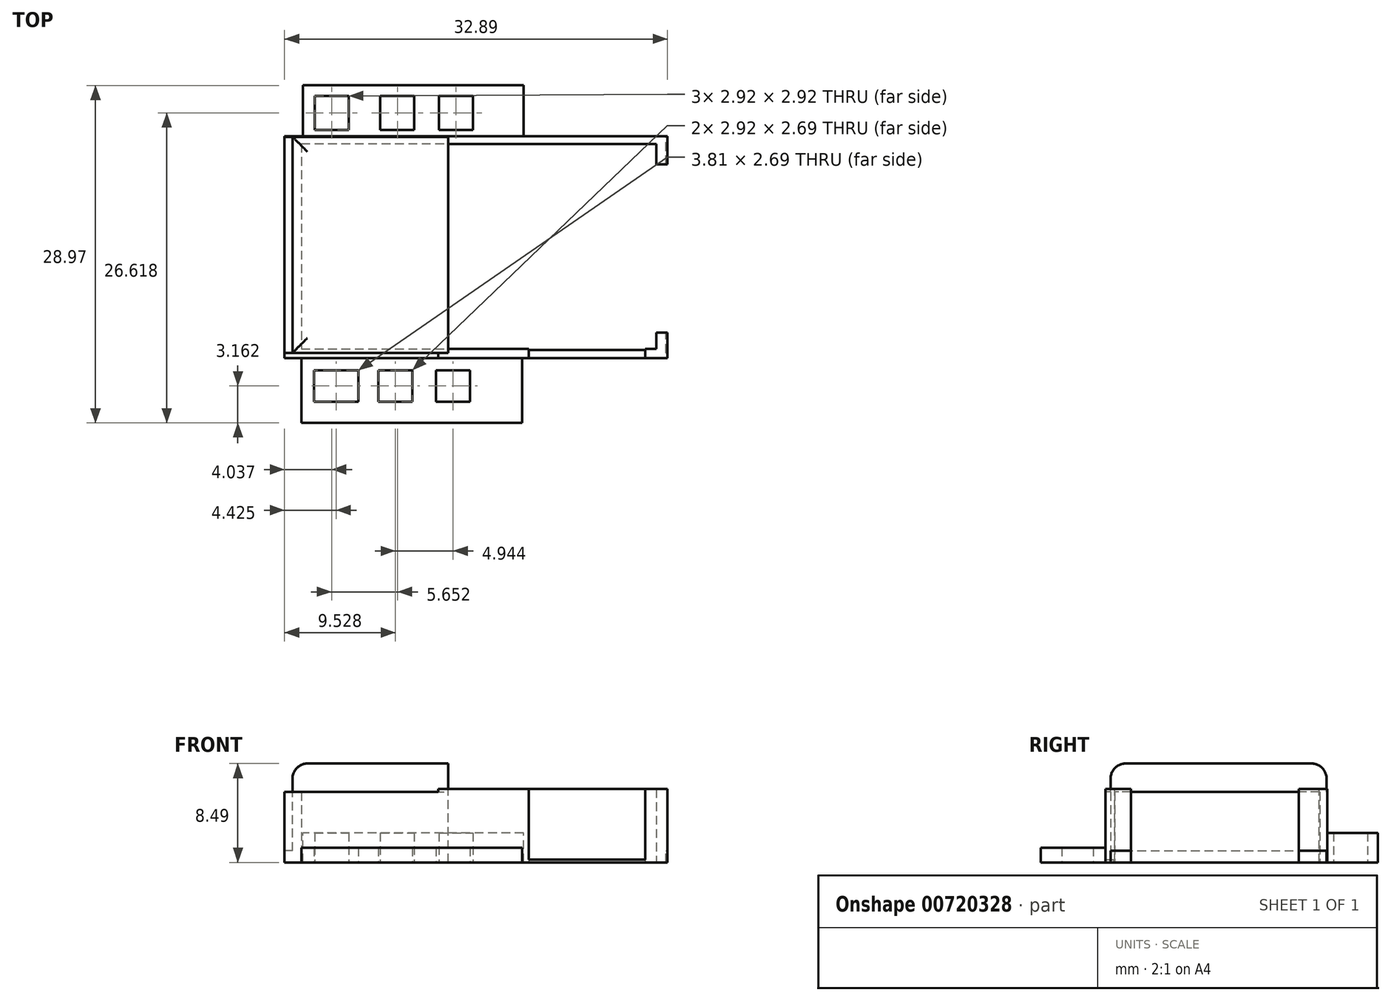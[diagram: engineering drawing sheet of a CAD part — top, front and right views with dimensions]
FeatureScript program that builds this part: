
annotation { "Feature Type Name" : "Feature", "Feature Type Description" : "" }
export const myFeature = defineFeature(function(context is Context, id is Id, definition is map)
    precondition{}
    {
        {
            var Q0;
            Q0=qCreatedBy(makeId("Top.planeOp"),FACE);
            var sketch = newSketch(context, id + "F0", { "sketchPlane" : qUnion([Q0])});
            skLineSegment(sketch, "E0.bottom", {"start": v(0, 0) * mm, "end": v(-33.73, 0) * mm});
            skLineSegment(sketch, "E0.top", {"start": v(0, 18.54) * mm, "end": v(-33.73, 18.54) * mm});
            skLineSegment(sketch, "E0.left", {"start": v(0, 0) * mm, "end": v(0, 18.54) * mm});
            skLineSegment(sketch, "E0.right", {"start": v(-33.73, 0) * mm, "end": v(-33.73, 18.54) * mm});
            skSolve(sketch);
        }
        {
            var Q0;
            Q0=makeQuery(id+"F0.imprint","IMPRINT",FACE,{"disambiguationData":[TD([[makeQuery(id+"F0.imprint","IMPRINT",EDGE,{"derivedFrom":sQuery(id+"F0.wireOp",EDGE,"E0.bottom")}),-1.0]])]});
            extrude(context, id + "F1", {"entities" : qUnion([Q0]), "depth" : 1 * mm, "offsetDistance" : 25.4 * mm});
        }
        {
            var Q0;
            Q0=qCreatedBy(makeId("Top.planeOp"),FACE);
            var sketch = newSketch(context, id + "F2", { "sketchPlane" : qUnion([Q0])});
            skLineSegment(sketch, "E1", {"start": v(0, 18.18) * mm, "end": v(-0.25, 18.18) * mm});
            skLineSegment(sketch, "E2", {"start": v(0, 0) * mm, "end": v(-1.24, 0) * mm});
            skLineSegment(sketch, "E3.bottom", {"start": v(-0.25, 16.18) * mm, "end": v(-2.75, 16.18) * mm});
            skLineSegment(sketch, "E3.top", {"start": v(-0.25, 1.75) * mm, "end": v(-2.75, 1.75) * mm});
            skLineSegment(sketch, "E3.left", {"start": v(-0.25, 16.18) * mm, "end": v(-0.25, 1.75) * mm});
            skLineSegment(sketch, "E3.right", {"start": v(-2.75, 16.18) * mm, "end": v(-2.75, 1.75) * mm});
            skSolve(sketch);
        }
        {
            var Q0;
            Q0 = qSketchRegion(id + "F2", true);
            extrude(context, id + "F3", {"entities" : qUnion([Q0]), "operationType" : NewBodyOperationType.ADD, "depth" : 7 * mm, "offsetDistance" : 25.4 * mm});
        }
        {
            var Q0;
            Q0=makeQuery(id+"F1.opExtrude","CAP_FACE",FACE,{"disambiguationData":[OSD([sQuery(id+"F0.wireOp",EDGE,"E0.bottom"),sQuery(id+"F0.wireOp",EDGE,"E0.top"),sQuery(id+"F0.wireOp",EDGE,"E0.left"),sQuery(id+"F0.wireOp",EDGE,"E0.right")])],"isStart":false});
            var sketch = newSketch(context, id + "F4", { "sketchPlane" : qUnion([Q0])});
            skLineSegment(sketch, "E4", {"start": v(0, 0) * mm, "end": v(-2.75, 0) * mm});
            skLineSegment(sketch, "E5.bottom", {"start": v(-2.75, 0) * mm, "end": v(-12.75, 0) * mm});
            skLineSegment(sketch, "E5.top", {"start": v(-2.75, 3) * mm, "end": v(-12.75, 3) * mm});
            skLineSegment(sketch, "E5.left", {"start": v(-2.75, 0) * mm, "end": v(-2.75, 3) * mm});
            skLineSegment(sketch, "E5.right", {"start": v(-12.75, 0) * mm, "end": v(-12.75, 3) * mm});
            skLineSegment(sketch, "E6", {"start": v(-2.75, 3) * mm, "end": v(-2.75, 4) * mm});
            skLineSegment(sketch, "E7", {"start": v(-12.75, 3) * mm, "end": v(-7.75, 3) * mm});
            skSolve(sketch);
        }
        {
            var Q0;
            {var subQ3=sQuery(id+"F4.wireOp",EDGE,"E5.bottom");Q0=makeQuery(id+"F4.imprint","IMPRINT",FACE,{"disambiguationData":[TD([[makeQuery(id+"F4.imprint","IMPRINT",EDGE,{"derivedFrom":subQ3}),-1.0]])]});}
            extrude(context, id + "F5", {"entities" : qUnion([Q0]), "operationType" : NewBodyOperationType.ADD, "depth" : 7.5 * mm, "offsetDistance" : 25.4 * mm});
        }
        {
            var Q0;
            Q0=makeQuery(id+"F1.opExtrude","CAP_FACE",FACE,{"disambiguationData":[OSD([sQuery(id+"F0.wireOp",EDGE,"E0.bottom"),sQuery(id+"F0.wireOp",EDGE,"E0.top"),sQuery(id+"F0.wireOp",EDGE,"E0.left"),sQuery(id+"F0.wireOp",EDGE,"E0.right")])],"isStart":false});
            var sketch = newSketch(context, id + "F6", { "sketchPlane" : qUnion([Q0])});
            skLineSegment(sketch, "E8", {"start": v(0, 18.54) * mm, "end": v(-2.73, 18.54) * mm});
            skLineSegment(sketch, "E9.bottom", {"start": v(-2.73, 18.54) * mm, "end": v(-8.73, 18.54) * mm});
            skLineSegment(sketch, "E9.top", {"start": v(-2.73, 15.54) * mm, "end": v(-8.73, 15.54) * mm});
            skLineSegment(sketch, "E9.left", {"start": v(-2.73, 18.54) * mm, "end": v(-2.73, 15.54) * mm});
            skLineSegment(sketch, "E9.right", {"start": v(-8.73, 18.54) * mm, "end": v(-8.73, 15.54) * mm});
            skSolve(sketch);
        }
        {
            var Q0;
            Q0 = qSketchRegion(id + "F6", true);
            extrude(context, id + "F7", {"entities" : qUnion([Q0]), "operationType" : NewBodyOperationType.ADD, "depth" : 3.75 * mm, "offsetDistance" : 25.4 * mm});
        }
        {
            var Q0;
            {var subQ0=sQuery(id+"F0.wireOp",EDGE,"E0.top");var subQ1=sQuery(id+"F0.wireOp",EDGE,"E0.right");var subQ2=sQuery(id+"F0.wireOp",EDGE,"E0.bottom");Q0=makeQuery(id+"F7.boolean.opBoolean","SPLIT",FACE,{"disambiguationData":[TD([makeQuery(id+"F1.opExtrude","SWEPT_FACE",FACE,{"disambiguationData":[OSD([subQ1])]})])],"derivedFrom":makeQuery(id+"F1.opExtrude","CAP_FACE",FACE,{"disambiguationData":[OSD([subQ2,subQ0,sQuery(id+"F0.wireOp",EDGE,"E0.left"),subQ1])],"isStart":false})});}
            var sketch = newSketch(context, id + "F8", { "sketchPlane" : qUnion([Q0])});
            skLineSegment(sketch, "E10", {"start": v(-12.75, 3) * mm, "end": v(-8.75, 3) * mm});
            skLineSegment(sketch, "E11.bottom", {"start": v(-8.75, 3) * mm, "end": v(-14.75, 3) * mm});
            skLineSegment(sketch, "E11.top", {"start": v(-8.75, 6.75) * mm, "end": v(-14.75, 6.75) * mm});
            skLineSegment(sketch, "E11.left", {"start": v(-8.75, 3) * mm, "end": v(-8.75, 6.75) * mm});
            skLineSegment(sketch, "E11.right", {"start": v(-14.75, 3) * mm, "end": v(-14.75, 6.75) * mm});
            skSolve(sketch);
        }
        {
            var Q0;
            Q0 = qSketchRegion(id + "F8", true);
            extrude(context, id + "F9", {"entities" : qUnion([Q0]), "operationType" : NewBodyOperationType.ADD, "depth" : 7.5 * mm, "offsetDistance" : 25.4 * mm});
        }
        {
            var Q0;
            {var subQ0=sQuery(id+"F0.wireOp",EDGE,"E0.top");var subQ1=sQuery(id+"F0.wireOp",EDGE,"E0.right");var subQ2=sQuery(id+"F0.wireOp",EDGE,"E0.bottom");Q0=makeQuery(id+"F7.boolean.opBoolean","SPLIT",FACE,{"disambiguationData":[TD([makeQuery(id+"F1.opExtrude","SWEPT_FACE",FACE,{"disambiguationData":[OSD([subQ1])]})])],"derivedFrom":makeQuery(id+"F1.opExtrude","CAP_FACE",FACE,{"disambiguationData":[OSD([subQ2,subQ0,sQuery(id+"F0.wireOp",EDGE,"E0.left"),subQ1])],"isStart":false})});}
            var sketch = newSketch(context, id + "F10", { "sketchPlane" : qUnion([Q0])});
            skLineSegment(sketch, "E12", {"start": v(-14.73, 7.77) * mm, "end": v(-9.77, 12.72) * mm});
            skLineSegment(sketch, "E13", {"start": v(-9.77, 12.72) * mm, "end": v(-14.73, 17.68) * mm});
            skLineSegment(sketch, "E14", {"start": v(-14.73, 17.68) * mm, "end": v(-19.68, 12.72) * mm});
            skLineSegment(sketch, "E15", {"start": v(-19.68, 12.72) * mm, "end": v(-14.73, 7.77) * mm});
            skSolve(sketch);
        }
        {
            var Q0;
            Q0=makeQuery(id+"F10.imprint","IMPRINT",FACE,{"disambiguationData":[TD([[makeQuery(id+"F10.imprint","IMPRINT",EDGE,{"derivedFrom":sQuery(id+"F10.wireOp",EDGE,"E12")}),1.0]])]});
            extrude(context, id + "F11", {"entities" : qUnion([Q0]), "operationType" : NewBodyOperationType.ADD, "depth" : 3 * mm, "offsetDistance" : 25.4 * mm});
        }
        {
            var Q0;
            Q0=makeQuery(id+"F9.boolean.opBoolean","MERGE",FACE,{"derivedFrom":[makeQuery(id+"F5.opExtrude","CAP_FACE",FACE,{"disambiguationData":[OSD([sQuery(id+"F4.wireOp",EDGE,"E5.bottom"),sQuery(id+"F4.wireOp",EDGE,"E5.top"),sQuery(id+"F4.wireOp",EDGE,"E5.left"),sQuery(id+"F4.wireOp",EDGE,"E5.right"),sQuery(id+"F4.wireOp",EDGE,"E7")])],"isStart":false}),makeQuery(id+"F9.opExtrude","CAP_FACE",FACE,{"disambiguationData":[OSD([sQuery(id+"F8.wireOp",EDGE,"E11.bottom"),sQuery(id+"F8.wireOp",EDGE,"E11.top"),sQuery(id+"F8.wireOp",EDGE,"E11.left"),sQuery(id+"F8.wireOp",EDGE,"E11.right")])],"isStart":false})]});
            var sketch = newSketch(context, id + "F12", { "sketchPlane" : qUnion([Q0])});
            skLineSegment(sketch, "E16", {"start": v(-14.75, 3) * mm, "end": v(-15.75, 3) * mm});
            skLineSegment(sketch, "E17", {"start": v(-14.75, 6.75) * mm, "end": v(-15.75, 6.75) * mm});
            skLineSegment(sketch, "E18", {"start": v(-15.75, 3) * mm, "end": v(-15.75, 0) * mm});
            skLineSegment(sketch, "E19", {"start": v(-15.75, 0) * mm, "end": v(-15.75, 3) * mm});
            skPoint(sketch, "E20.endSnap0", {"position": v(-7.75, 0) * mm});
            skSolve(sketch);
        }
        {
            var Q0;
            {var subQ0=sQuery(id+"F0.wireOp",EDGE,"E0.top");var subQ1=sQuery(id+"F0.wireOp",EDGE,"E0.right");var subQ2=sQuery(id+"F0.wireOp",EDGE,"E0.bottom");Q0=makeQuery(id+"F7.boolean.opBoolean","SPLIT",FACE,{"disambiguationData":[TD([makeQuery(id+"F1.opExtrude","SWEPT_FACE",FACE,{"disambiguationData":[OSD([subQ1])]})])],"derivedFrom":makeQuery(id+"F1.opExtrude","CAP_FACE",FACE,{"disambiguationData":[OSD([subQ2,subQ0,sQuery(id+"F0.wireOp",EDGE,"E0.left"),subQ1])],"isStart":false})});}
            var sketch = newSketch(context, id + "F13", { "sketchPlane" : qUnion([Q0])});
            skLineSegment(sketch, "E21", {"start": v(-19.68, 0) * mm, "end": v(-19.68, 18.54) * mm});
            skSolve(sketch);
        }
        {
            var Q0;
            Q0=sQuery(id+"F13.wireOp",EDGE,"E21");
            extrude(context, id + "F14", {"bodyType" : ToolBodyType.SURFACE, "surfaceEntities" : qUnion([Q0]), "depth" : 7.5 * mm, "offsetDistance" : 25.4 * mm});
        }
        {
            var Q0;
            Q0=makeQuery(id+"F14.opExtrude","SWEPT_FACE",FACE,{"disambiguationData":[OSD([sQuery(id+"F13.wireOp",EDGE,"E21")])]});
            var Q1;
            Q1=makeQuery(id+"F11.opExtrude","SWEPT_FACE",FACE,{"disambiguationData":[OSD([sQuery(id+"F10.wireOp",EDGE,"E15")])]});
            extrude(context, id + "F15", {"entities" : qUnion([Q0, Q1]), "operationType" : NewBodyOperationType.ADD, "oppositeDirection" : true, "depth" : 13.36 * mm, "offsetDistance" : 25.4 * mm});
        }
        {
            var Q0;
            {var subQ0=sQuery(id+"F13.wireOp",EDGE,"E21");Q0=makeQuery(id+"F15.opExtrude","CAP_EDGE",EDGE,{"disambiguationData":[OSD([subQ0]),TDD([makeQuery(id+"F14.opExtrude","CAP_EDGE",EDGE,{"disambiguationData":[OSD([subQ0])],"isStart":false})])],"isStart":false});}
            var Q1;
            {var subQ0=sQuery(id+"F13.wireOp",VERTEX,"E21.start");Q1=makeQuery(id+"F15.opExtrude","SWEPT_EDGE",EDGE,{"disambiguationData":[OSD([subQ0]),TDD([makeQuery(id+"F14.opExtrude","CAP_VERTEX",VERTEX,{"disambiguationData":[OSD([subQ0])],"isStart":false})])]});}
            var Q2;
            {var subQ0=sQuery(id+"F13.wireOp",VERTEX,"E21.end");Q2=makeQuery(id+"F15.opExtrude","SWEPT_EDGE",EDGE,{"disambiguationData":[OSD([subQ0]),TDD([makeQuery(id+"F14.opExtrude","CAP_VERTEX",VERTEX,{"disambiguationData":[OSD([subQ0])],"isStart":false})])]});}
            fillet(context, id + "F16", {"entities" : qUnion([Q0, Q1, Q2]), "radius" : 1.27 * mm, "tangentPropagation" : true, "rho" : .4, "crossSection" : FilletCrossSection.CONIC, "allowEdgeOverflow" : false});
        }
        {
            var Q0;
            Q0=qCreatedBy(makeId("Top.planeOp"),FACE);
            var sketch = newSketch(context, id + "F17", { "sketchPlane" : qUnion([Q0])});
            skLineSegment(sketch, "E22", {"start": v(-0.84, 9.07) * mm, "end": v(-20.52, 9.07) * mm});
            skLineSegment(sketch, "E23", {"start": v(-0.84, 9.07) * mm, "end": v(-0.84, 19.66) * mm});
            skSolve(sketch);
        }
        {
            var Q0;
            Q0 = qSketchRegion(id + "F17", true);
            var Q1;
            Q1=sQuery(id+"F17.wireOp",EDGE,"E22");
            extrude(context, id + "F18", {"entities" : qUnion([Q0]), "bodyType" : ToolBodyType.SURFACE, "surfaceEntities" : qUnion([Q1]), "depth" : 6.3 * mm, "offsetDistance" : 25.4 * mm});
        }
        {
            var Q0;
            Q0=makeQuery(id+"F18.opExtrude","SWEPT_FACE",FACE,{"disambiguationData":[OSD([sQuery(id+"F17.wireOp",EDGE,"E22")])]});
            extrude(context, id + "F19", {"entities" : qUnion([Q0]), "operationType" : NewBodyOperationType.ADD, "endBound" : BoundingType.SYMMETRIC, "depth" : 19.05 * mm, "offsetDistance" : 25.4 * mm});
        }
        {
            var Q0;
            {var subQ0=sQuery(id+"F17.wireOp",EDGE,"E22");Q0=makeQuery(id+"F19.opExtrude","SWEPT_FACE",FACE,{"disambiguationData":[OSD([subQ0]),TDD([makeQuery(id+"F18.opExtrude","CAP_EDGE",EDGE,{"disambiguationData":[OSD([subQ0])],"isStart":false})])]});}
            var sketch = newSketch(context, id + "F20", { "sketchPlane" : qUnion([Q0])});
            skPoint(sketch, "E24.firstSnap0", {"position": v(-20.54, 0.34) * mm});
            skPoint(sketch, "E24.oppositeSnap0", {"position": v(-1.8, 1.75) * mm});
            skPoint(sketch, "E24.oppositeSnap1", {"position": v(-20.54, 17.92) * mm});
            skLineSegment(sketch, "E24.bottom", {"start": v(-19.68, 0.34) * mm, "end": v(-1.8, 0.34) * mm});
            skLineSegment(sketch, "E24.top", {"start": v(-19.68, 17.92) * mm, "end": v(-1.8, 17.92) * mm});
            skLineSegment(sketch, "E24.left", {"start": v(-19.68, 0.34) * mm, "end": v(-19.68, 17.92) * mm});
            skLineSegment(sketch, "E24.right", {"start": v(-1.8, 0.34) * mm, "end": v(-1.8, 17.92) * mm});
            skSolve(sketch);
        }
        {
            var Q0;
            Q0 = qSketchRegion(id + "F20", true);
            extrude(context, id + "F21", {"entities" : qUnion([Q0]), "operationType" : NewBodyOperationType.REMOVE, "oppositeDirection" : true, "depth" : 25.4 * mm, "offsetDistance" : 25.4 * mm});
        }
        {
            var Q0;
            {var subQ1=sQuery(id+"F4.wireOp",EDGE,"E5.left");var subQ3=sQuery(id+"F4.wireOp",EDGE,"E5.bottom");Q0=makeQuery(id+"F19.boolean.opBoolean","SPLIT",FACE,{"disambiguationData":[TD([makeQuery(id+"F5.opExtrude","SWEPT_FACE",FACE,{"disambiguationData":[OSD([subQ1])]})])],"derivedFrom":makeQuery(id+"F15.boolean.opBoolean","MERGE",FACE,{"derivedFrom":[makeQuery(id+"F5.boolean.opBoolean","MERGE",FACE,{"derivedFrom":[makeQuery(id+"F1.opExtrude","SWEPT_FACE",FACE,{"disambiguationData":[OSD([sQuery(id+"F0.wireOp",EDGE,"E0.bottom")])]}),makeQuery(id+"F5.opExtrude","SWEPT_FACE",FACE,{"disambiguationData":[OSD([subQ3])]})]}),makeQuery(id+"F15.opExtrude","SWEPT_FACE",FACE,{"disambiguationData":[OSD([sQuery(id+"F13.wireOp",VERTEX,"E21.start")])]})]})});}
            var sketch = newSketch(context, id + "F22", { "sketchPlane" : qUnion([Q0])});
            skLineSegment(sketch, "E25.bottom", {"start": v(-12.75, 6.3) * mm, "end": v(-2.75, 6.3) * mm});
            skLineSegment(sketch, "E25.top", {"start": v(-12.75, 0) * mm, "end": v(-2.75, 0) * mm});
            skLineSegment(sketch, "E25.left", {"start": v(-12.75, 6.3) * mm, "end": v(-12.75, 0) * mm});
            skLineSegment(sketch, "E25.right", {"start": v(-2.75, 6.3) * mm, "end": v(-2.75, 0) * mm});
            skSolve(sketch);
        }
        {
            var Q0;
            Q0 = qSketchRegion(id + "F22", true);
            extrude(context, id + "F23", {"entities" : qUnion([Q0]), "operationType" : NewBodyOperationType.REMOVE, "depth" : 25.4 * mm, "offsetDistance" : 25.4 * mm});
        }
        {
            var Q0;
            Q0=makeQuery(id+"F12.imprint","IMPRINT",FACE,{"disambiguationData":[TD([[makeQuery(id+"F12.imprint","IMPRINT",EDGE,{"derivedFrom":makeQuery(id+"F5.opExtrude","CAP_EDGE",EDGE,{"disambiguationData":[OSD([sQuery(id+"F4.wireOp",EDGE,"E5.bottom")])],"isStart":false})}),-1.0]])]});
            extrude(context, id + "F24", {"entities" : qUnion([Q0]), "operationType" : NewBodyOperationType.REMOVE, "oppositeDirection" : true, "depth" : 25.4 * mm, "offsetDistance" : 25.4 * mm});
        }
        {
            var Q0;
            {var subQ0=sQuery(id+"F17.wireOp",EDGE,"E22");Q0=makeQuery(id+"F19.boolean.opBoolean","MERGE",FACE,{"derivedFrom":[makeQuery(id+"F1.opExtrude","CAP_FACE",FACE,{"disambiguationData":[OSD([sQuery(id+"F0.wireOp",EDGE,"E0.bottom"),sQuery(id+"F0.wireOp",EDGE,"E0.top"),sQuery(id+"F0.wireOp",EDGE,"E0.left"),sQuery(id+"F0.wireOp",EDGE,"E0.right")])],"isStart":true}),makeQuery(id+"F19.opExtrude","SWEPT_FACE",FACE,{"disambiguationData":[OSD([subQ0]),TDD([makeQuery(id+"F18.opExtrude","CAP_EDGE",EDGE,{"disambiguationData":[OSD([subQ0])],"isStart":true})])]})]});}
            var sketch = newSketch(context, id + "F25", { "sketchPlane" : qUnion([Q0])});
            skLineSegment(sketch, "E26.bottom", {"start": v(-12.75, -0.25) * mm, "end": v(-2.75, -0.25) * mm});
            skLineSegment(sketch, "E26.top", {"start": v(-12.75, 0.46) * mm, "end": v(-2.75, 0.46) * mm});
            skLineSegment(sketch, "E26.left", {"start": v(-12.75, -0.25) * mm, "end": v(-12.75, 0.46) * mm});
            skLineSegment(sketch, "E26.right", {"start": v(-2.75, -0.25) * mm, "end": v(-2.75, 0.46) * mm});
            skLineSegment(sketch, "E27.bottom", {"start": v(-0.84, -18.54) * mm, "end": v(0, -18.54) * mm});
            skLineSegment(sketch, "E27.top", {"start": v(-0.84, -18.6) * mm, "end": v(0, -18.6) * mm});
            skLineSegment(sketch, "E27.left", {"start": v(-0.84, -18.54) * mm, "end": v(-0.84, -18.6) * mm});
            skLineSegment(sketch, "E27.right", {"start": v(0, -18.54) * mm, "end": v(0, -18.6) * mm});
            skLineSegment(sketch, "E28.bottom", {"start": v(-33.73, -18.54) * mm, "end": v(-20.52, -18.54) * mm});
            skLineSegment(sketch, "E28.top", {"start": v(-33.73, -18.6) * mm, "end": v(-20.52, -18.6) * mm});
            skLineSegment(sketch, "E28.left", {"start": v(-33.73, -18.54) * mm, "end": v(-33.73, -18.6) * mm});
            skLineSegment(sketch, "E28.right", {"start": v(-20.52, -18.54) * mm, "end": v(-20.52, -18.6) * mm});
            skSolve(sketch);
        }
        {
            var Q0;
            Q0=makeQuery(id+"F25.imprint","IMPRINT",FACE,{"disambiguationData":[TD([[makeQuery(id+"F25.imprint","IMPRINT",EDGE,{"derivedFrom":sQuery(id+"F25.wireOp",EDGE,"E26.bottom")}),1.0]])]});
            extrude(context, id + "F26", {"entities" : qUnion([Q0]), "operationType" : NewBodyOperationType.ADD, "oppositeDirection" : true, "depth" : 0.25 * mm, "offsetDistance" : 25.4 * mm});
        }
        {
            var Q0;
            {var subQ0=sQuery(id+"F17.wireOp",EDGE,"E22");Q0=makeQuery(id+"F26.boolean.opBoolean","MERGE",FACE,{"derivedFrom":[makeQuery(id+"F19.boolean.opBoolean","MERGE",FACE,{"derivedFrom":[makeQuery(id+"F1.opExtrude","CAP_FACE",FACE,{"disambiguationData":[OSD([sQuery(id+"F0.wireOp",EDGE,"E0.bottom"),sQuery(id+"F0.wireOp",EDGE,"E0.top"),sQuery(id+"F0.wireOp",EDGE,"E0.left"),sQuery(id+"F0.wireOp",EDGE,"E0.right")])],"isStart":true}),makeQuery(id+"F19.opExtrude","SWEPT_FACE",FACE,{"disambiguationData":[OSD([subQ0]),TDD([makeQuery(id+"F18.opExtrude","CAP_EDGE",EDGE,{"disambiguationData":[OSD([subQ0])],"isStart":true})])]})]}),makeQuery(id+"F26.opExtrude","CAP_FACE",FACE,{"disambiguationData":[OSD([sQuery(id+"F25.wireOp",EDGE,"E26.bottom"),sQuery(id+"F25.wireOp",EDGE,"E26.top"),sQuery(id+"F25.wireOp",EDGE,"E26.left"),sQuery(id+"F25.wireOp",EDGE,"E26.right")])],"isStart":true})]});}
            var sketch = newSketch(context, id + "F27", { "sketchPlane" : qUnion([Q0])});
            skLineSegment(sketch, "E29.bottom", {"start": v(-20.52, 0) * mm, "end": v(-33.73, 0) * mm});
            skLineSegment(sketch, "E29.top", {"start": v(-20.52, 0.45) * mm, "end": v(-33.73, 0.45) * mm});
            skLineSegment(sketch, "E29.left", {"start": v(-20.52, 0) * mm, "end": v(-20.52, 0.45) * mm});
            skLineSegment(sketch, "E29.right", {"start": v(-33.73, 0) * mm, "end": v(-33.73, 0.45) * mm});
            skLineSegment(sketch, "E30.bottom", {"start": v(-20.52, -18.6) * mm, "end": v(-33.73, -18.6) * mm});
            skLineSegment(sketch, "E30.top", {"start": v(-20.52, -18.54) * mm, "end": v(-33.73, -18.54) * mm});
            skLineSegment(sketch, "E30.left", {"start": v(-20.52, -18.6) * mm, "end": v(-20.52, -18.54) * mm});
            skLineSegment(sketch, "E30.right", {"start": v(-33.73, -18.6) * mm, "end": v(-33.73, -18.54) * mm});
            skSolve(sketch);
        }
        {
            var Q0;
            Q0 = qSketchRegion(id + "F27", true);
            extrude(context, id + "F28", {"entities" : qUnion([Q0]), "operationType" : NewBodyOperationType.ADD, "oppositeDirection" : true, "depth" : 6.05 * mm, "offsetDistance" : 25.4 * mm});
        }
        {
            var Q0;
            {var subQ0=sQuery(id+"F17.wireOp",EDGE,"E22");Q0=makeQuery(id+"F28.boolean.opBoolean","MERGE",FACE,{"derivedFrom":[makeQuery(id+"F26.boolean.opBoolean","MERGE",FACE,{"derivedFrom":[makeQuery(id+"F19.boolean.opBoolean","MERGE",FACE,{"derivedFrom":[makeQuery(id+"F1.opExtrude","CAP_FACE",FACE,{"disambiguationData":[OSD([sQuery(id+"F0.wireOp",EDGE,"E0.bottom"),sQuery(id+"F0.wireOp",EDGE,"E0.top"),sQuery(id+"F0.wireOp",EDGE,"E0.left"),sQuery(id+"F0.wireOp",EDGE,"E0.right")])],"isStart":true}),makeQuery(id+"F19.opExtrude","SWEPT_FACE",FACE,{"disambiguationData":[OSD([subQ0]),TDD([makeQuery(id+"F18.opExtrude","CAP_EDGE",EDGE,{"disambiguationData":[OSD([subQ0])],"isStart":true})])]})]}),makeQuery(id+"F26.opExtrude","CAP_FACE",FACE,{"disambiguationData":[OSD([sQuery(id+"F25.wireOp",EDGE,"E26.bottom"),sQuery(id+"F25.wireOp",EDGE,"E26.top"),sQuery(id+"F25.wireOp",EDGE,"E26.left"),sQuery(id+"F25.wireOp",EDGE,"E26.right")])],"isStart":true})]}),makeQuery(id+"F28.opExtrude","CAP_FACE",FACE,{"disambiguationData":[OSD([sQuery(id+"F27.wireOp",EDGE,"E29.bottom"),sQuery(id+"F27.wireOp",EDGE,"E29.top"),sQuery(id+"F27.wireOp",EDGE,"E29.left"),sQuery(id+"F27.wireOp",EDGE,"E29.right")])],"isStart":true}),makeQuery(id+"F28.opExtrude","CAP_FACE",FACE,{"disambiguationData":[OSD([sQuery(id+"F27.wireOp",EDGE,"E30.bottom"),sQuery(id+"F27.wireOp",EDGE,"E30.top"),sQuery(id+"F27.wireOp",EDGE,"E30.left"),sQuery(id+"F27.wireOp",EDGE,"E30.right")])],"isStart":true})]});}
            var sketch = newSketch(context, id + "F29", { "sketchPlane" : qUnion([Q0])});
            skLineSegment(sketch, "E31", {"start": v(-33.73, -18.6) * mm, "end": v(-33.73, -17.87) * mm});
            skLineSegment(sketch, "E32.bottom", {"start": v(-32.29, -17.96) * mm, "end": v(-19.68, -17.96) * mm});
            skLineSegment(sketch, "E32.top", {"start": v(-32.29, -0.34) * mm, "end": v(-19.68, -0.34) * mm});
            skLineSegment(sketch, "E32.left", {"start": v(-32.29, -17.96) * mm, "end": v(-32.29, -0.34) * mm});
            skLineSegment(sketch, "E32.right", {"start": v(-19.68, -17.96) * mm, "end": v(-19.68, -0.34) * mm});
            skSolve(sketch);
        }
        {
            var Q0;
            Q0=makeQuery(id+"F29.imprint","IMPRINT",FACE,{"disambiguationData":[TD([[makeQuery(id+"F29.imprint","IMPRINT",EDGE,{"derivedFrom":sQuery(id+"F29.wireOp",EDGE,"E32.bottom")}),1.0]])]});
            extrude(context, id + "F30", {"entities" : qUnion([Q0]), "operationType" : NewBodyOperationType.REMOVE, "oppositeDirection" : true, "depth" : 6.05 * mm, "offsetDistance" : 25.4 * mm});
        }
        {
            var Q0;
            Q0=makeQuery(id+"F3.opExtrude","SWEPT_FACE",FACE,{"disambiguationData":[OSD([sQuery(id+"F2.wireOp",EDGE,"E3.left")])]});
            var sketch = newSketch(context, id + "F31", { "sketchPlane" : qUnion([Q0])});
            skLineSegment(sketch, "E33.bottom", {"start": v(1.75, 7) * mm, "end": v(16.18, 7) * mm});
            skLineSegment(sketch, "E33.top", {"start": v(1.75, 1) * mm, "end": v(16.18, 1) * mm});
            skLineSegment(sketch, "E33.left", {"start": v(1.75, 7) * mm, "end": v(1.75, 1) * mm});
            skLineSegment(sketch, "E33.right", {"start": v(16.18, 7) * mm, "end": v(16.18, 1) * mm});
            skSolve(sketch);
        }
        {
            var Q0;
            Q0 = qSketchRegion(id + "F31", true);
            extrude(context, id + "F32", {"entities" : qUnion([Q0]), "operationType" : NewBodyOperationType.REMOVE, "oppositeDirection" : true, "depth" : 2.54 * mm, "offsetDistance" : 25.4 * mm});
        }
        {
            var Q0;
            {var subQ0=sQuery(id+"F0.wireOp",EDGE,"E0.left");var subQ1=sQuery(id+"F0.wireOp",EDGE,"E0.top");var subQ2=sQuery(id+"F0.wireOp",EDGE,"E0.bottom");Q0=makeQuery(id+"F32.boolean.opBoolean","MERGE",FACE,{"derivedFrom":[makeQuery(id+"F7.boolean.opBoolean","SPLIT",FACE,{"disambiguationData":[TD([makeQuery(id+"F1.opExtrude","SWEPT_FACE",FACE,{"disambiguationData":[OSD([subQ0])]})])],"derivedFrom":makeQuery(id+"F1.opExtrude","CAP_FACE",FACE,{"disambiguationData":[OSD([subQ2,subQ1,subQ0,sQuery(id+"F0.wireOp",EDGE,"E0.right")])],"isStart":false})}),makeQuery(id+"F32.opExtrude","SWEPT_FACE",FACE,{"disambiguationData":[OSD([sQuery(id+"F31.wireOp",EDGE,"E33.top")])]})]});}
            var sketch = newSketch(context, id + "F33", { "sketchPlane" : qUnion([Q0])});
            skLineSegment(sketch, "E34.bottom", {"start": v(-1.8, 16.18) * mm, "end": v(-0.84, 16.18) * mm});
            skLineSegment(sketch, "E34.top", {"start": v(-1.8, 1.75) * mm, "end": v(-0.84, 1.75) * mm});
            skLineSegment(sketch, "E34.left", {"start": v(-1.8, 16.18) * mm, "end": v(-1.8, 1.75) * mm});
            skLineSegment(sketch, "E34.right", {"start": v(-0.84, 16.18) * mm, "end": v(-0.84, 1.75) * mm});
            skSolve(sketch);
        }
        {
            var Q0;
            Q0 = qSketchRegion(id + "F33", true);
            extrude(context, id + "F34", {"entities" : qUnion([Q0]), "operationType" : NewBodyOperationType.REMOVE, "oppositeDirection" : true, "depth" : 1.27 * mm, "offsetDistance" : 25.4 * mm});
        }
        {
            var Q0;
            {var subQ0=sQuery(id+"F17.wireOp",EDGE,"E22");Q0=makeQuery(id+"F28.boolean.opBoolean","MERGE",FACE,{"derivedFrom":[makeQuery(id+"F26.boolean.opBoolean","MERGE",FACE,{"derivedFrom":[makeQuery(id+"F19.boolean.opBoolean","MERGE",FACE,{"derivedFrom":[makeQuery(id+"F1.opExtrude","CAP_FACE",FACE,{"disambiguationData":[OSD([sQuery(id+"F0.wireOp",EDGE,"E0.bottom"),sQuery(id+"F0.wireOp",EDGE,"E0.top"),sQuery(id+"F0.wireOp",EDGE,"E0.left"),sQuery(id+"F0.wireOp",EDGE,"E0.right")])],"isStart":true}),makeQuery(id+"F19.opExtrude","SWEPT_FACE",FACE,{"disambiguationData":[OSD([subQ0]),TDD([makeQuery(id+"F18.opExtrude","CAP_EDGE",EDGE,{"disambiguationData":[OSD([subQ0])],"isStart":true})])]})]}),makeQuery(id+"F26.opExtrude","CAP_FACE",FACE,{"disambiguationData":[OSD([sQuery(id+"F25.wireOp",EDGE,"E26.bottom"),sQuery(id+"F25.wireOp",EDGE,"E26.top"),sQuery(id+"F25.wireOp",EDGE,"E26.left"),sQuery(id+"F25.wireOp",EDGE,"E26.right")])],"isStart":true})]}),makeQuery(id+"F28.opExtrude","CAP_FACE",FACE,{"disambiguationData":[OSD([sQuery(id+"F27.wireOp",EDGE,"E29.bottom"),sQuery(id+"F27.wireOp",EDGE,"E29.top"),sQuery(id+"F27.wireOp",EDGE,"E29.left"),sQuery(id+"F27.wireOp",EDGE,"E29.right")])],"isStart":true}),makeQuery(id+"F28.opExtrude","CAP_FACE",FACE,{"disambiguationData":[OSD([sQuery(id+"F27.wireOp",EDGE,"E30.bottom"),sQuery(id+"F27.wireOp",EDGE,"E30.top"),sQuery(id+"F27.wireOp",EDGE,"E30.left"),sQuery(id+"F27.wireOp",EDGE,"E30.right")])],"isStart":true})]});}
            var sketch = newSketch(context, id + "F35", { "sketchPlane" : qUnion([Q0])});
            skLineSegment(sketch, "E35.bottom", {"start": v(-19.7, -17.4) * mm, "end": v(-32.29, -17.4) * mm});
            skLineSegment(sketch, "E35.top", {"start": v(-19.7, -17.92) * mm, "end": v(-32.29, -17.92) * mm});
            skLineSegment(sketch, "E35.left", {"start": v(-19.7, -17.4) * mm, "end": v(-19.7, -17.92) * mm});
            skLineSegment(sketch, "E35.right", {"start": v(-32.29, -17.4) * mm, "end": v(-32.29, -17.92) * mm});
            skSolve(sketch);
        }
        {
            var Q0;
            Q0 = qSketchRegion(id + "F35", true);
            extrude(context, id + "F36", {"entities" : qUnion([Q0]), "operationType" : NewBodyOperationType.REMOVE, "oppositeDirection" : true, "depth" : 3.8 * mm, "offsetDistance" : 25.4 * mm});
        }
        {
            var Q0;
            {var subQ0=sQuery(id+"F17.wireOp",EDGE,"E22");Q0=makeQuery(id+"F28.boolean.opBoolean","MERGE",FACE,{"derivedFrom":[makeQuery(id+"F26.boolean.opBoolean","MERGE",FACE,{"derivedFrom":[makeQuery(id+"F19.boolean.opBoolean","MERGE",FACE,{"derivedFrom":[makeQuery(id+"F1.opExtrude","CAP_FACE",FACE,{"disambiguationData":[OSD([sQuery(id+"F0.wireOp",EDGE,"E0.bottom"),sQuery(id+"F0.wireOp",EDGE,"E0.top"),sQuery(id+"F0.wireOp",EDGE,"E0.left"),sQuery(id+"F0.wireOp",EDGE,"E0.right")])],"isStart":true}),makeQuery(id+"F19.opExtrude","SWEPT_FACE",FACE,{"disambiguationData":[OSD([subQ0]),TDD([makeQuery(id+"F18.opExtrude","CAP_EDGE",EDGE,{"disambiguationData":[OSD([subQ0])],"isStart":true})])]})]}),makeQuery(id+"F26.opExtrude","CAP_FACE",FACE,{"disambiguationData":[OSD([sQuery(id+"F25.wireOp",EDGE,"E26.bottom"),sQuery(id+"F25.wireOp",EDGE,"E26.top"),sQuery(id+"F25.wireOp",EDGE,"E26.left"),sQuery(id+"F25.wireOp",EDGE,"E26.right")])],"isStart":true})]}),makeQuery(id+"F28.opExtrude","CAP_FACE",FACE,{"disambiguationData":[OSD([sQuery(id+"F27.wireOp",EDGE,"E29.bottom"),sQuery(id+"F27.wireOp",EDGE,"E29.top"),sQuery(id+"F27.wireOp",EDGE,"E29.left"),sQuery(id+"F27.wireOp",EDGE,"E29.right")])],"isStart":true}),makeQuery(id+"F28.opExtrude","CAP_FACE",FACE,{"disambiguationData":[OSD([sQuery(id+"F27.wireOp",EDGE,"E30.bottom"),sQuery(id+"F27.wireOp",EDGE,"E30.top"),sQuery(id+"F27.wireOp",EDGE,"E30.left"),sQuery(id+"F27.wireOp",EDGE,"E30.right")])],"isStart":true})]});}
            var sketch = newSketch(context, id + "F37", { "sketchPlane" : qUnion([Q0])});
            skLineSegment(sketch, "E36.bottom", {"start": v(-32.29, -0.34) * mm, "end": v(-13.32, -0.34) * mm});
            skLineSegment(sketch, "E36.top", {"start": v(-32.29, 6) * mm, "end": v(-13.32, 6) * mm});
            skLineSegment(sketch, "E36.left", {"start": v(-32.29, -0.34) * mm, "end": v(-32.29, 6) * mm});
            skLineSegment(sketch, "E36.right", {"start": v(-13.32, -0.34) * mm, "end": v(-13.32, 6) * mm});
            skLineSegment(sketch, "E37.bottom", {"start": v(-31.21, 1.5) * mm, "end": v(-27.4, 1.5) * mm});
            skLineSegment(sketch, "E37.top", {"start": v(-31.21, 4.2) * mm, "end": v(-27.4, 4.2) * mm});
            skLineSegment(sketch, "E37.left", {"start": v(-31.21, 1.5) * mm, "end": v(-31.21, 4.2) * mm});
            skLineSegment(sketch, "E37.right", {"start": v(-27.4, 1.5) * mm, "end": v(-27.4, 4.2) * mm});
            skLineSegment(sketch, "E38.bottom", {"start": v(-25.66, 1.5) * mm, "end": v(-22.74, 1.5) * mm});
            skLineSegment(sketch, "E38.top", {"start": v(-25.66, 4.2) * mm, "end": v(-22.74, 4.2) * mm});
            skLineSegment(sketch, "E38.left", {"start": v(-25.66, 1.5) * mm, "end": v(-25.66, 4.2) * mm});
            skLineSegment(sketch, "E38.right", {"start": v(-22.74, 1.5) * mm, "end": v(-22.74, 4.2) * mm});
            skLineSegment(sketch, "E39.bottom", {"start": v(-20.72, 1.5) * mm, "end": v(-17.8, 1.5) * mm});
            skLineSegment(sketch, "E39.top", {"start": v(-20.72, 4.2) * mm, "end": v(-17.8, 4.2) * mm});
            skLineSegment(sketch, "E39.left", {"start": v(-20.72, 1.5) * mm, "end": v(-20.72, 4.2) * mm});
            skLineSegment(sketch, "E39.right", {"start": v(-17.8, 1.5) * mm, "end": v(-17.8, 4.2) * mm});
            skSolve(sketch);
        }
        {
            var Q0;
            {var subQ9=sQuery(id+"F0.wireOp",EDGE,"E0.left");Q0=makeQuery(id+"F37.imprint","IMPRINT",FACE,{"disambiguationData":[TD([[makeQuery(id+"F37.imprint","IMPRINT",EDGE,{"derivedFrom":makeQuery(id+"F1.opExtrude","CAP_EDGE",EDGE,{"disambiguationData":[OSD([subQ9])],"isStart":true})}),-1.0]])]});}
            var sketch = newSketch(context, id + "F38", { "sketchPlane" : qUnion([Q0])});
            skLineSegment(sketch, "E40.bottom", {"start": v(-32.16, -18.02) * mm, "end": v(-13.2, -18.02) * mm});
            skLineSegment(sketch, "E40.top", {"start": v(-32.16, -22.96) * mm, "end": v(-13.2, -22.96) * mm});
            skLineSegment(sketch, "E40.left", {"start": v(-32.16, -18.02) * mm, "end": v(-32.16, -22.96) * mm});
            skLineSegment(sketch, "E40.right", {"start": v(-13.2, -18.02) * mm, "end": v(-13.2, -22.96) * mm});
            skLineSegment(sketch, "E41.bottom", {"start": v(-31.15, -19.15) * mm, "end": v(-28.23, -19.15) * mm});
            skLineSegment(sketch, "E41.top", {"start": v(-31.15, -22.07) * mm, "end": v(-28.23, -22.07) * mm});
            skLineSegment(sketch, "E41.left", {"start": v(-31.15, -19.15) * mm, "end": v(-31.15, -22.07) * mm});
            skLineSegment(sketch, "E41.right", {"start": v(-28.23, -19.15) * mm, "end": v(-28.23, -22.07) * mm});
            skLineSegment(sketch, "E42.bottom", {"start": v(-25.5, -19.15) * mm, "end": v(-22.58, -19.15) * mm});
            skLineSegment(sketch, "E42.top", {"start": v(-25.5, -22.07) * mm, "end": v(-22.58, -22.07) * mm});
            skLineSegment(sketch, "E42.left", {"start": v(-25.5, -19.15) * mm, "end": v(-25.5, -22.07) * mm});
            skLineSegment(sketch, "E42.right", {"start": v(-22.58, -19.15) * mm, "end": v(-22.58, -22.07) * mm});
            skLineSegment(sketch, "E43.bottom", {"start": v(-20.47, -19.15) * mm, "end": v(-17.55, -19.15) * mm});
            skLineSegment(sketch, "E43.top", {"start": v(-20.47, -22.07) * mm, "end": v(-17.55, -22.07) * mm});
            skLineSegment(sketch, "E43.left", {"start": v(-20.47, -19.15) * mm, "end": v(-20.47, -22.07) * mm});
            skLineSegment(sketch, "E43.right", {"start": v(-17.55, -19.15) * mm, "end": v(-17.55, -22.07) * mm});
            skSolve(sketch);
        }
        {
            var Q0;
            Q0 = qSketchRegion(id + "F37", true);
            extrude(context, id + "F39", {"entities" : qUnion([Q0]), "operationType" : NewBodyOperationType.ADD, "oppositeDirection" : true, "depth" : 1.27 * mm, "offsetDistance" : 25.4 * mm});
        }
        {
            var Q0;
            Q0 = qSketchRegion(id + "F38", true);
            extrude(context, id + "F40", {"entities" : qUnion([Q0]), "operationType" : NewBodyOperationType.ADD, "oppositeDirection" : true, "depth" : 2.54 * mm, "offsetDistance" : 25.4 * mm});
        }
        {
            var Q0;
            Q0=makeQuery(id+"F1.opExtrude","SWEPT_FACE",FACE,{"disambiguationData":[OSD([sQuery(id+"F0.wireOp",EDGE,"E0.left")])]});
            var sketch = newSketch(context, id + "F41", { "sketchPlane" : qUnion([Q0])});
            skSolve(sketch);
        }
        {
            var Q0;
            Q0 = qSketchRegion(id + "F41", true);
            var Q1;
            {var subQ0=sQuery(id+"F0.wireOp",EDGE,"E0.left");Q1=makeQuery(id+"F41.imprint","IMPRINT",FACE,{"disambiguationData":[TD([[makeQuery(id+"F41.imprint","IMPRINT",EDGE,{"derivedFrom":makeQuery(id+"F1.opExtrude","CAP_EDGE",EDGE,{"disambiguationData":[OSD([subQ0])],"isStart":true})}),1.0]])]});}
            extrude(context, id + "F42", {"entities" : qUnion([Q0, Q1]), "operationType" : NewBodyOperationType.REMOVE, "oppositeDirection" : true, "depth" : 0.97 * mm, "offsetDistance" : 25.4 * mm});
        }
    });
